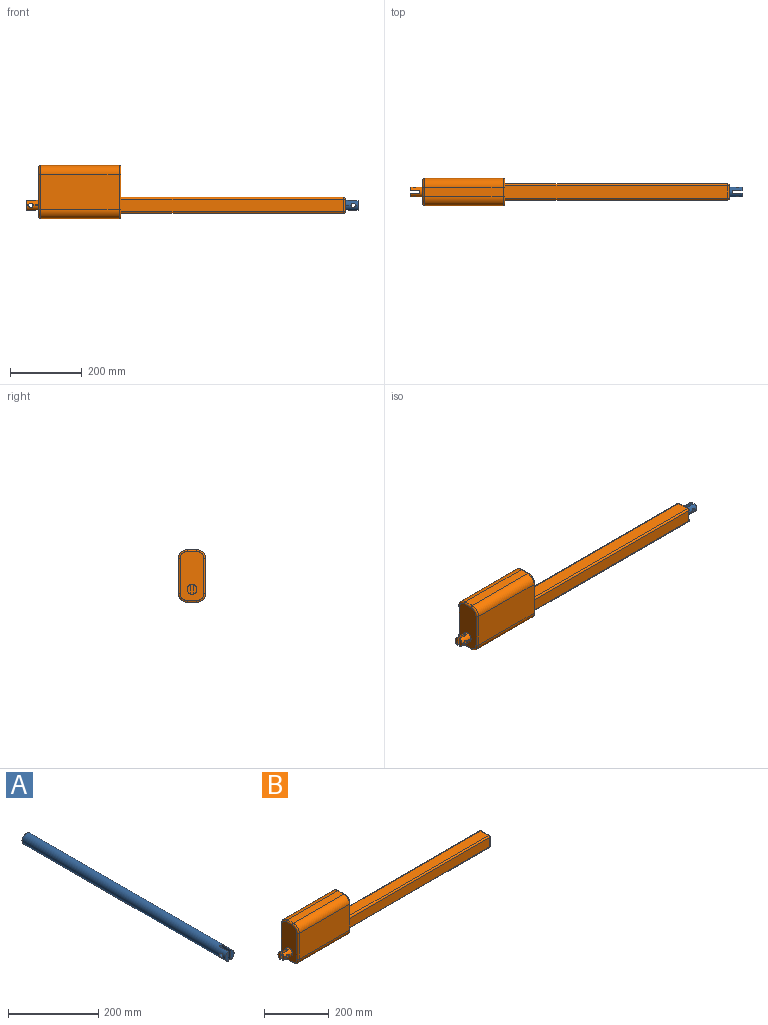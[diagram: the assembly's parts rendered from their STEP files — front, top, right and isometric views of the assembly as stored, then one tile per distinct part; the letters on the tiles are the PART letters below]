
ASSEMBLY  parts=2 mates=1
PART A: 12 faces, bbox 27.8x635.6x27.8 mm
  f0: plane 26.56x9.76mm, normal (0,-1,0), area 191.1mm2, adj f2,f6,f10
  f1: cylinder r=6.1mm len=12.2mm, axis (1,0,0), area 348.8mm2, adj f2,f3,f6,f10
  f2: cylinder r=13.9mm len=635.6mm, axis (0,1,0), area 54766.9mm2, adj f0,f1,f3,f4,f5,f6,f7,f8
  f3: plane 15.99x2.04mm, normal (1,0,0), area 32.5mm2, adj f1,f2,f7
  f4: plane 26.56x9.8mm, normal (0,-1,0), area 191.2mm2, adj f2,f9
  f5: plane 27.8x27.8mm, normal (0,1,0), area 607mm2, adj f2
  f6: plane 6.99x2.04mm, normal (1,0,0), area 14.1mm2, adj f0,f1,f2
  f7: plane 2.04x0.04mm, normal (0,-1,0), area 0.1mm2, adj f2,f3
  f8: cylinder r=6.1mm len=12.2mm, axis (1,0,0), area 349mm2, adj f2,f9
  f9: plane 27.5x26.56mm, normal (1,0,0), area 613.6mm2, adj f2,f4,f8,f11
  f10: plane 27.5x26.56mm, normal (-1,0,0), area 613.6mm2, adj f0,f1,f2,f11
  f11: plane 27.8x8.2mm, normal (0,-1,0), area 224.6mm2, adj f2,f9,f10
PART B: 56 faces, bbox 890.4x80.1x152.1 mm
  f0: plane 26.56x9.72mm, normal (-1,0,0), area 191mm2, adj f2,f11,f54
  f1: cylinder r=6.1mm len=12.2mm, axis (0,-1,0), area 348.6mm2, adj f2,f3,f11,f54
  f2: cylinder r=13.9mm len=35.6mm, axis (1,0,0), area 2342.7mm2, adj f0,f1,f3,f5,f10,f11,f12,f13
  f3: plane 16.09x3mm, normal (0,-1,0), area 47.9mm2, adj f1,f2,f12
  f4: plane 219x26mm, normal (0,0,1), area 5694mm2, adj f20,f22,f26,f34
  f5: plane 138x66mm, normal (-1,0,0), area 8157.6mm2, adj f2,f23,f24,f25,f26,f27,f28,f29
  f6: plane 219x26mm, normal (0,0,-1), area 5694mm2, adj f19,f21,f27,f35
  f7: plane 138x66mm, normal (1,0,0), area 6779.1mm2, adj f14,f15,f16,f17,f31,f32,f33,f34
  f8: plane 219x98mm, normal (0,-1,0), area 21462mm2, adj f21,f22,f30,f38
  f9: plane 219x98mm, normal (0,1,0), area 21462mm2, adj f19,f20,f23,f31
  f10: plane 26.56x9.8mm, normal (-1,0,0), area 191.2mm2, adj f2,f53
  f11: plane 7.09x3mm, normal (0,-1,0), area 20.9mm2, adj f0,f1,f2
  f12: plane 3x0.08mm, normal (-1,0,0), area 0.2mm2, adj f2,f3
  f13: cylinder r=6.1mm len=12.2mm, axis (0,-1,0), area 349mm2, adj f2,f53
  f14: plane 620.8x34.8mm, normal (0,-1,0), area 21603.8mm2, adj f7,f41,f47,f50
  f15: plane 620.8x34.8mm, normal (0,0,-1), area 21603.8mm2, adj f7,f44,f48,f50
  f16: plane 620.8x34.8mm, normal (0,1,0), area 21603.8mm2, adj f7,f39,f43,f44
  f17: plane 620.8x34.8mm, normal (0,0,1), area 21603.8mm2, adj f7,f39,f41,f42
  f18: plane 34.8x34.8mm, normal (1,0,0), area 604.1mm2, adj f42,f43,f47,f48,f51
  f19: cylinder r=25mm len=219mm, axis (1,0,0), area 8600.1mm2, adj f6,f9,f25,f33
  f20: cylinder r=25mm len=219mm, axis (-1,0,0), area 8600.1mm2, adj f4,f9,f24,f32
  f21: cylinder r=25mm len=219mm, axis (-1,0,0), area 8600.1mm2, adj f6,f8,f29,f37
  f22: cylinder r=25mm len=219mm, axis (1,0,0), area 8600.1mm2, adj f4,f8,f28,f36
  f23: cylinder r=5mm len=98mm, axis (0,0,-1), area 769.7mm2, adj f5,f9,f24,f25
  f24: torus R=20mm, axis (1,0,0), area 286mm2, adj f5,f20,f23,f26
  f25: torus R=20mm, axis (1,0,0), area 286mm2, adj f5,f19,f23,f27
  f26: cylinder r=5mm len=26mm, axis (0,-1,0), area 204.2mm2, adj f4,f5,f24,f28
  f27: cylinder r=5mm len=26mm, axis (0,1,0), area 204.2mm2, adj f5,f6,f25,f29
  f28: torus R=20mm, axis (1,0,0), area 286mm2, adj f5,f22,f26,f30
  f29: torus R=20mm, axis (1,0,0), area 286mm2, adj f5,f21,f27,f30
  f30: cylinder r=5mm len=98mm, axis (0,0,1), area 769.7mm2, adj f5,f8,f28,f29
  f31: cylinder r=5mm len=98mm, axis (0,0,1), area 769.7mm2, adj f7,f9,f32,f33
  f32: torus R=20mm, axis (1,0,0), area 286mm2, adj f7,f20,f31,f34
  f33: torus R=20mm, axis (1,0,0), area 286mm2, adj f7,f19,f31,f35
  f34: cylinder r=5mm len=26mm, axis (0,1,0), area 204.2mm2, adj f4,f7,f32,f36
  f35: cylinder r=5mm len=26mm, axis (0,-1,0), area 204.2mm2, adj f6,f7,f33,f37
  f36: torus R=20mm, axis (1,0,0), area 286mm2, adj f7,f22,f34,f38
  f37: torus R=20mm, axis (1,0,0), area 286mm2, adj f7,f21,f35,f38
  f38: cylinder r=5mm len=98mm, axis (0,0,-1), area 769.7mm2, adj f7,f8,f36,f37
  f39: cylinder r=5mm len=620.8mm, axis (-1,0,0), area 4875.8mm2, adj f7,f16,f17,f40
  f40: sphere r=5mm, area 39.3mm2, adj f39,f42,f43
  f41: cylinder r=5mm len=620.8mm, axis (1,0,0), area 4875.8mm2, adj f7,f14,f17,f45
  f42: cylinder r=5mm len=34.8mm, axis (0,1,0), area 273.3mm2, adj f17,f18,f40,f45
  f43: cylinder r=5mm len=34.8mm, axis (0,0,-1), area 273.3mm2, adj f16,f18,f40,f46
  f44: cylinder r=5mm len=620.8mm, axis (1,0,0), area 4875.8mm2, adj f7,f15,f16,f46
  f45: sphere r=5mm, area 39.3mm2, adj f41,f42,f47
  f46: sphere r=5mm, area 39.3mm2, adj f43,f44,f48
  f47: cylinder r=5mm len=34.8mm, axis (0,0,1), area 273.3mm2, adj f14,f18,f45,f49
  f48: cylinder r=5mm len=34.8mm, axis (0,-1,0), area 273.3mm2, adj f15,f18,f46,f49
  f49: sphere r=5mm, area 39.3mm2, adj f47,f48,f50
  f50: cylinder r=5mm len=620.8mm, axis (-1,0,0), area 4875.8mm2, adj f7,f14,f15,f49
  f51: cylinder r=13.9mm len=600mm, axis (1,0,0), area 52401.8mm2, adj f18,f52
  f52: plane 27.8x27.8mm, normal (1,0,0), area 607mm2, adj f51
  f53: plane 27.5x26.56mm, normal (0,-1,0), area 613.6mm2, adj f2,f10,f13,f55
  f54: plane 27.5x26.56mm, normal (0,1,0), area 613.6mm2, adj f0,f1,f2,f55
  f55: plane 27.8x8.2mm, normal (-1,0,0), area 224.6mm2, adj f2,f53,f54
PLACE A rot(axis=(0.71,-0.71,0),180deg) t=(314.42,88.25,-36.15)mm
PLACE B t=(-143.68,88.25,1.25)mm fixed
MATE slider A.f2 <-> B.f51  axis (-1,0,0) through (-3.38,88.25,-36.15)mm
